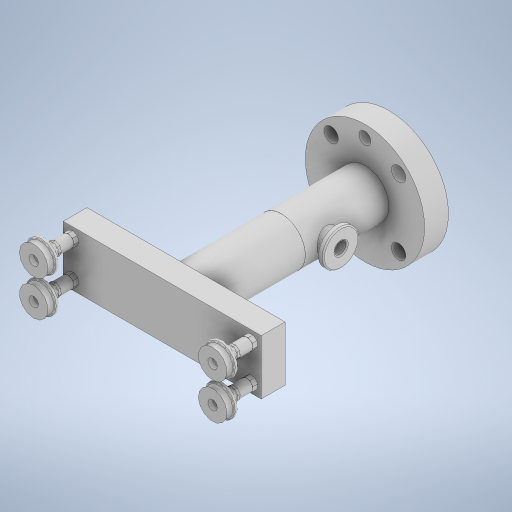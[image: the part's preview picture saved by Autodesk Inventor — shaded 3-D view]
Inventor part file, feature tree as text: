
AUTODESK INVENTOR PART (.ipt)
format: ipt  version: 2024 (Build 280153000, 153)  size: 944,128 bytes
history: native  units: mm
features: other x29, sketch x2
ambient origin geometry x8: Origin, YZ Plane, XZ Plane, XY Plane, X Axis, Y Axis, Z Axis, Center Point
bodies: Body1 (feature_tree), Body2 (feature_tree), Body3 (feature_tree), Body4 (feature_tree), Body5 (feature_tree), Body6 (feature_tree), Body7 (feature_tree), Body8 (feature_tree), Body9 (feature_tree), Body10 (feature_tree), Body11 (feature_tree), Body12 (feature_tree), Body13 (feature_tree), Body14 (feature_tree)
feature tree (31):
  other  "ENSAMBLAJE_VENTOSA_2.iam"
  other  "ACOPLE.ipt:1"
  other  "TORNILLO_B.ipt:4"
  other  "TUBO_METALICO_B.ipt:4"
  other  "VENTOSA_B.ipt:4"
  other  "UNION_B.ipt:1"
  other  "TORNILLO_B_MIR.ipt:1"
  other  "TUBO_METALICO_B_MIR.ipt:1"
  other  "VENTOSA_B_MIR.ipt:1"
  other  "TORNILLO_B_MIR1.ipt:1"
  other  "TUBO_METALICO_B_MIR1.ipt:1"
  other  "VENTOSA_B_MIR1.ipt:1"
  other  "TORNILLO_B_MIR_MIR.ipt:1"
  other  "TUBO_METALICO_B_MIR_MIR.ipt:1"
  other  "VENTOSA_B_MIR_MIR.ipt:1"
  other  "Sólido1"
  sketch  "Boceto 1"  dims[d0=10.0mm]
  sketch  "Boceto 2"
  other  "Sólido2"
  other  "Sólido3"
  other  "Sólido4"
  other  "Sólido5"
  other  "Sólido6"
  other  "Sólido7"
  other  "Sólido8"
  other  "Sólido9"
  other  "Sólido10"
  other  "Sólido11"
  other  "Sólido12"
  other  "Sólido13"
  other  "Sólido14"
